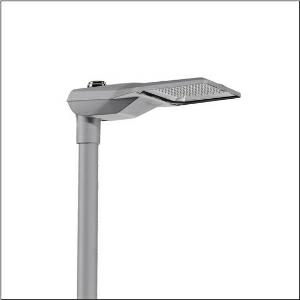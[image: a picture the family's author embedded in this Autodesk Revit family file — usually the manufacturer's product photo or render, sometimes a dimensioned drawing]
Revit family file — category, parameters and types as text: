
# Revit family: streetlight_sl_21_midi___stw1_0a_5xe7e47n08nb_2a9b
name_source: partatom
category: Lighting Fixtures
units: mm (PartAtom-declared; Revit-internal decimal feet)

## family parameters
Cut with Voids When Loaded = No
Host = Face
Light Source = No
Part Type = Normal
Room Calculation Point = No
Round Connector Dimension = Use Diameter
Shared = No

## types (1)
- --- (1 x LED, 23710 lm, 151.2 W, 4000K)
    Apparent Load = 151 VA
    CIE Flux Codes = 39 75 98 100 100
    Color Rendering = 70
    Color Temperature = 4000K
    Default Elevation = 1800 mm
    Description = Streetlight SL 21 midi, mast luminaire, primary light control with lens, of PMMA, primary optical cover: cover, of toughened safety glass, transparent, light distribution: STW1.0a, light emission: direct distribution, primary light characteristic: asymmetric, installation type: side-entry, LED, 3G 2.5mm², High Power LED, rated luminous flux: 23.710lm, luminous efficacy: 157lm/W, light colour: 740, colour temperature: 4000K, control gear: NEMA (7pin), control: overheat protection, pre-setting: linear dimming characteristic, constant luminous flux control, time-dependent luminous flux control, flexible luminous flux parameterisation, mains connection: 220..240V, AC, 50/60Hz, connection cable pre-assembled, cable length: 12,5m, wiring characteristics: H05VV-F, start of lifetime: 151W, end of service life: 157W, reduction: 70W, luminaire housing, of diecast aluminium (EN AC-44300), powder-coated, SITECO metallic grey (DB 702S), corrosivity category C5 high according to DIN EN ISO 12944, multi-level sealing system, sealing non-destructively replaceable, inclination adjustable: 0°, 5°, 10°, 15°, length: 644mm, width: 335mm, height: 110mm, spigot size: 42mm (side-entry), mounting height: 4..8m, protection rating (complete): IP66, insulation class (complete): insulation class I (protective earthing), certification: CE, ENEC, ENEC+, VDE, impact resistance: IK10, permissible operating ambient temperature for outdoor applications: -40..+50°C, standard-compliant lighting for roads and squares, packaging unit: 1 piece

Light Distribution: STW1.0a
    Height = 111 mm
    Lamp = 1 x LED
    Lamp Light Flux = 23710 lm
    Lamp Power = 151.2 W
    Lamp count = 1
    Length = 644 mm
    Luminous efficacy = 157 lm/W
    Manufacturer = Siteco
    ModVariant = No
    Model = 5XE7E47N08NB
    Number of Poles = 1
    OnlyDefault = Yes
    Power Factor = 1
    Product Name = Streetlight SL 21 midi | STW1.0a
    Product group = mast luminaire | pylon top
    ProductGroupID = 6100
    Protection Class = Protection class I
    Protection Degree = IP 66
    RLX_Detail_Level = 1
    RLX_Emergency_Light_Flux = 0 lm
    RLX_Emergency_Type = 0
    RLX_Emergency_Type_DB = No
    RlxData = <blob elided: 26673 chars, md5=d90d6cda>
    Socket = socket
    Standby Power = 0 W
    System Light Flux = 23710 lm
    System Power = 151 W
    Type Comments = factory setting: luminous flux: 100 % | dim-lin: 254 | 802 mA
    Type Image = l_1294377.jpg
    URL = http://relux.com
    VarID = @adj_134391
    Voltage = 0 V
    Weight = 0.00 kg
    Width = 336 mm

## geometry (parser evidence)
native form markers: Blend x4, Sweep x11
no freeform markers — native parametric forms only
